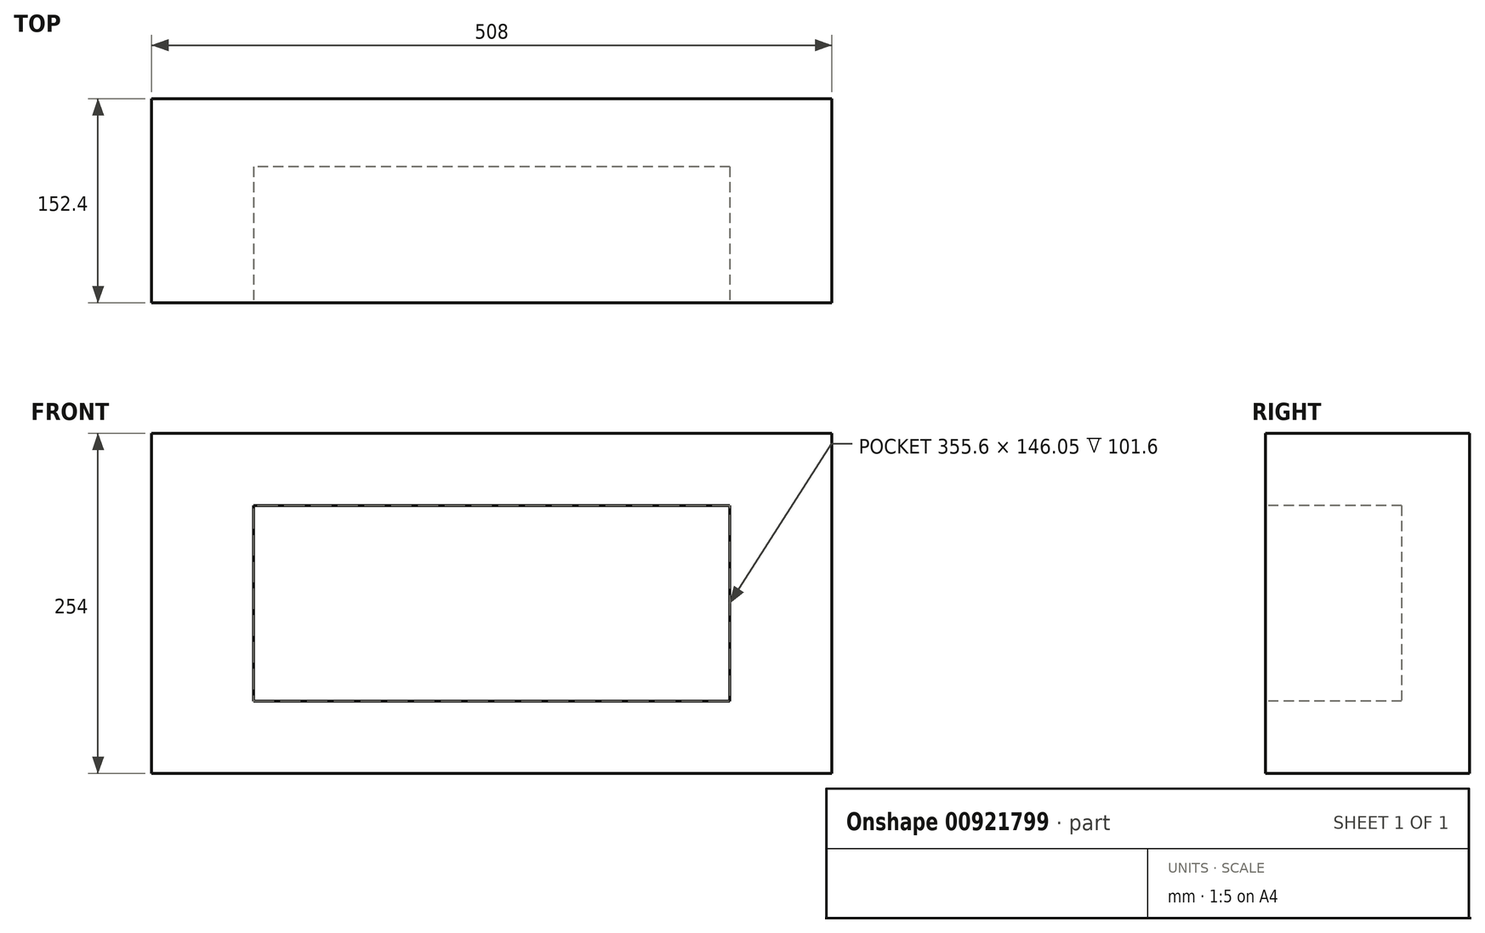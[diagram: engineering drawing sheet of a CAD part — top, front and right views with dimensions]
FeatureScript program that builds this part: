
annotation { "Feature Type Name" : "Feature", "Feature Type Description" : "" }
export const myFeature = defineFeature(function(context is Context, id is Id, definition is map)
    precondition{}
    {
        {
            var Q0;
            Q0=qCreatedBy(makeId("Front.planeOp"),FACE);
            var sketch = newSketch(context, id + "F0", { "sketchPlane" : qUnion([Q0])});
            skPoint(sketch, "E0.middle", {"position": v(0, 0) * mm});
            skLineSegment(sketch, "E1.bottom", {"start": v(254, -127) * mm, "end": v(-254, -127) * mm});
            skLineSegment(sketch, "E1.top", {"start": v(254, 127) * mm, "end": v(-254, 127) * mm});
            skLineSegment(sketch, "E1.left", {"start": v(254, -127) * mm, "end": v(254, 127) * mm});
            skLineSegment(sketch, "E1.right", {"start": v(-254, -127) * mm, "end": v(-254, 127) * mm});
            skSolve(sketch);
        }
        {
            var Q0;
            Q0 = qSketchRegion(id + "F0", true);
            extrude(context, id + "F1", {"entities" : qUnion([Q0]), "depth" : 152.4 * mm, "offsetDistance" : 25.4 * mm});
        }
        {
            var Q0;
            Q0=makeQuery(id+"F1.opExtrude","CAP_FACE",FACE,{"disambiguationData":[OSD([sQuery(id+"F0.wireOp",EDGE,"E1.bottom"),sQuery(id+"F0.wireOp",EDGE,"E1.top"),sQuery(id+"F0.wireOp",EDGE,"E1.left"),sQuery(id+"F0.wireOp",EDGE,"E1.right")])],"isStart":false});
            var sketch = newSketch(context, id + "F2", { "sketchPlane" : qUnion([Q0])});
            skLineSegment(sketch, "E2.bottom", {"start": v(177.8, 73.03) * mm, "end": v(-177.8, 73.03) * mm});
            skLineSegment(sketch, "E2.top", {"start": v(177.8, -73.03) * mm, "end": v(-177.8, -73.03) * mm});
            skLineSegment(sketch, "E2.left", {"start": v(177.8, 73.03) * mm, "end": v(177.8, -73.03) * mm});
            skLineSegment(sketch, "E2.right", {"start": v(-177.8, 73.03) * mm, "end": v(-177.8, -73.03) * mm});
            skPoint(sketch, "E2.middle", {"position": v(0, 0) * mm});
            skSolve(sketch);
        }
        {
            var Q0;
            Q0 = qSketchRegion(id + "F2", true);
            extrude(context, id + "F3", {"entities" : qUnion([Q0]), "operationType" : NewBodyOperationType.REMOVE, "oppositeDirection" : true, "depth" : 101.6 * mm, "offsetDistance" : 25.4 * mm});
        }
    });
